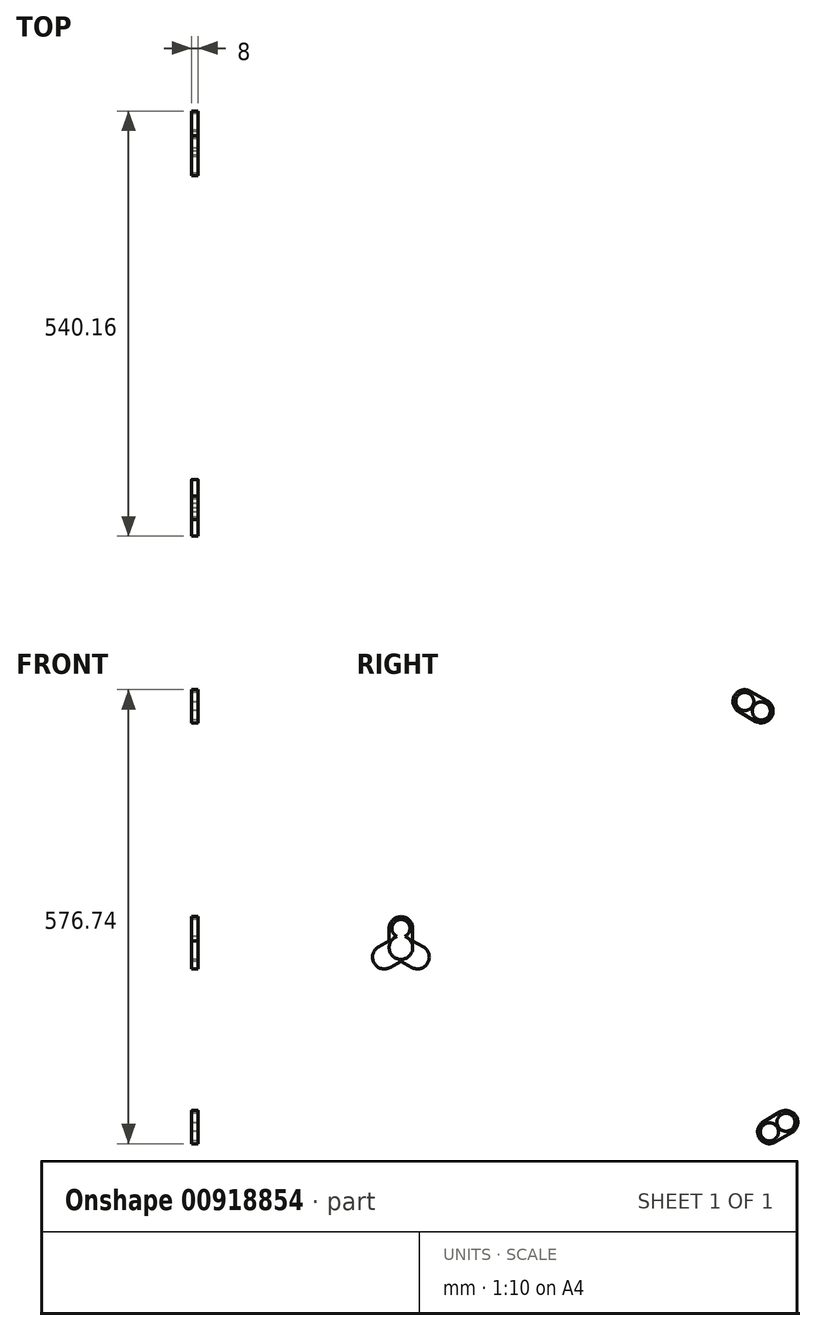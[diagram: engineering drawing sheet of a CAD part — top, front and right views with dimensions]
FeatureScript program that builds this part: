
annotation { "Feature Type Name" : "Feature", "Feature Type Description" : "" }
export const myFeature = defineFeature(function(context is Context, id is Id, definition is map)
    precondition{}
    {
        {
            var Q0;
            Q0=qCreatedBy(makeId("Right.planeOp"),FACE);
            var sketch = newSketch(context, id + "F0", { "sketchPlane" : qUnion([Q0])});
            skCircle(sketch, "E0", {"center": v(-305.76, -11.71) * mm, "radius": 11.43 * mm});
            skCircle(sketch, "E1", {"center": v(-305.76, -35.98) * mm, "radius": 11.43 * mm});
            skArc(sketch, "E2", {"start": v(-290.76, -35.98) * mm, "mid": v(-305.76, -50.98) * mm, "end": v(-320.76, -35.98) * mm});
            skArc(sketch, "E3", {"start": v(-290.76, -11.71) * mm, "mid": v(-305.76, 3.29) * mm, "end": v(-320.76, -11.71) * mm});
            skLineSegment(sketch, "E4", {"start": v(-320.76, -11.71) * mm, "end": v(-320.76, -35.98) * mm});
            skLineSegment(sketch, "E5", {"start": v(-290.76, -11.71) * mm, "end": v(-290.76, -35.98) * mm});
            skLineSegment(sketch, "E6.1.0", {"start": v(169.88, -283.08) * mm, "end": v(190.9, -270.94) * mm});
            skArc(sketch, "E6.1.1", {"start": v(154.88, -257.1) * mm, "mid": v(149.39, -277.59) * mm, "end": v(169.88, -283.08) * mm});
            skCircle(sketch, "E6.1.2", {"center": v(183.4, -257.95) * mm, "radius": 11.43 * mm});
            skArc(sketch, "E6.1.3", {"start": v(175.9, -244.96) * mm, "mid": v(196.39, -250.45) * mm, "end": v(190.9, -270.94) * mm});
            skLineSegment(sketch, "E6.1.4", {"start": v(154.88, -257.1) * mm, "end": v(175.9, -244.96) * mm});
            skCircle(sketch, "E6.1.5", {"center": v(162.38, -270.09) * mm, "radius": 11.43 * mm});
            skLineSegment(sketch, "E6.2.0", {"start": v(159.57, 277.5) * mm, "end": v(138.55, 289.64) * mm});
            skArc(sketch, "E6.2.1", {"start": v(144.57, 251.52) * mm, "mid": v(165.06, 257.01) * mm, "end": v(159.57, 277.5) * mm});
            skCircle(sketch, "E6.2.2", {"center": v(131.05, 276.65) * mm, "radius": 11.43 * mm});
            skArc(sketch, "E6.2.3", {"start": v(123.55, 263.66) * mm, "mid": v(118.06, 284.15) * mm, "end": v(138.55, 289.64) * mm});
            skLineSegment(sketch, "E6.2.4", {"start": v(144.57, 251.52) * mm, "end": v(123.55, 263.66) * mm});
            skCircle(sketch, "E6.2.5", {"center": v(152.07, 264.51) * mm, "radius": 11.43 * mm});
            skPoint(sketch, "E6.center", {"position": v(2.9, -5.76) * mm});
            skLineSegment(sketch, "E7.1.0", {"start": v(-319.27, -61.1) * mm, "end": v(-298.26, -48.97) * mm});
            skArc(sketch, "E7.1.1", {"start": v(-334.27, -35.13) * mm, "mid": v(-339.76, -55.62) * mm, "end": v(-319.27, -61.1) * mm});
            skLineSegment(sketch, "E7.1.2", {"start": v(-334.27, -35.13) * mm, "end": v(-313.26, -23) * mm});
            skArc(sketch, "E7.1.3", {"start": v(-313.26, -23) * mm, "mid": v(-292.77, -28.48) * mm, "end": v(-298.26, -48.97) * mm});
            skCircle(sketch, "E7.1.4", {"center": v(-326.77, -48.12) * mm, "radius": 11.43 * mm});
            skLineSegment(sketch, "E7.2.0", {"start": v(-277.24, -35.13) * mm, "end": v(-298.26, -23) * mm});
            skArc(sketch, "E7.2.1", {"start": v(-292.24, -61.1) * mm, "mid": v(-271.75, -55.62) * mm, "end": v(-277.24, -35.13) * mm});
            skLineSegment(sketch, "E7.2.2", {"start": v(-292.24, -61.1) * mm, "end": v(-313.26, -48.97) * mm});
            skArc(sketch, "E7.2.3", {"start": v(-313.26, -48.97) * mm, "mid": v(-318.75, -28.48) * mm, "end": v(-298.26, -23) * mm});
            skCircle(sketch, "E7.2.4", {"center": v(-284.74, -48.12) * mm, "radius": 11.43 * mm});
            skSolve(sketch);
        }
        {
            var Q0;
            Q0 = qSketchRegion(id + "F0", true);
            var Q1;
            {var subQ9=sQuery(id+"F0.wireOp",EDGE,"E2");Q1=makeQuery(id+"F0.imprint","IMPRINT",FACE,{"disambiguationData":[TD([[makeQuery(id+"F0.imprint","IMPRINT",EDGE,{"derivedFrom":subQ9}),-1.0]])]});}
            extrude(context, id + "F1", {"entities" : qUnion([Q0, Q1]), "depth" : 8 * mm, "offsetDistance" : 25 * mm});
        }
    });
